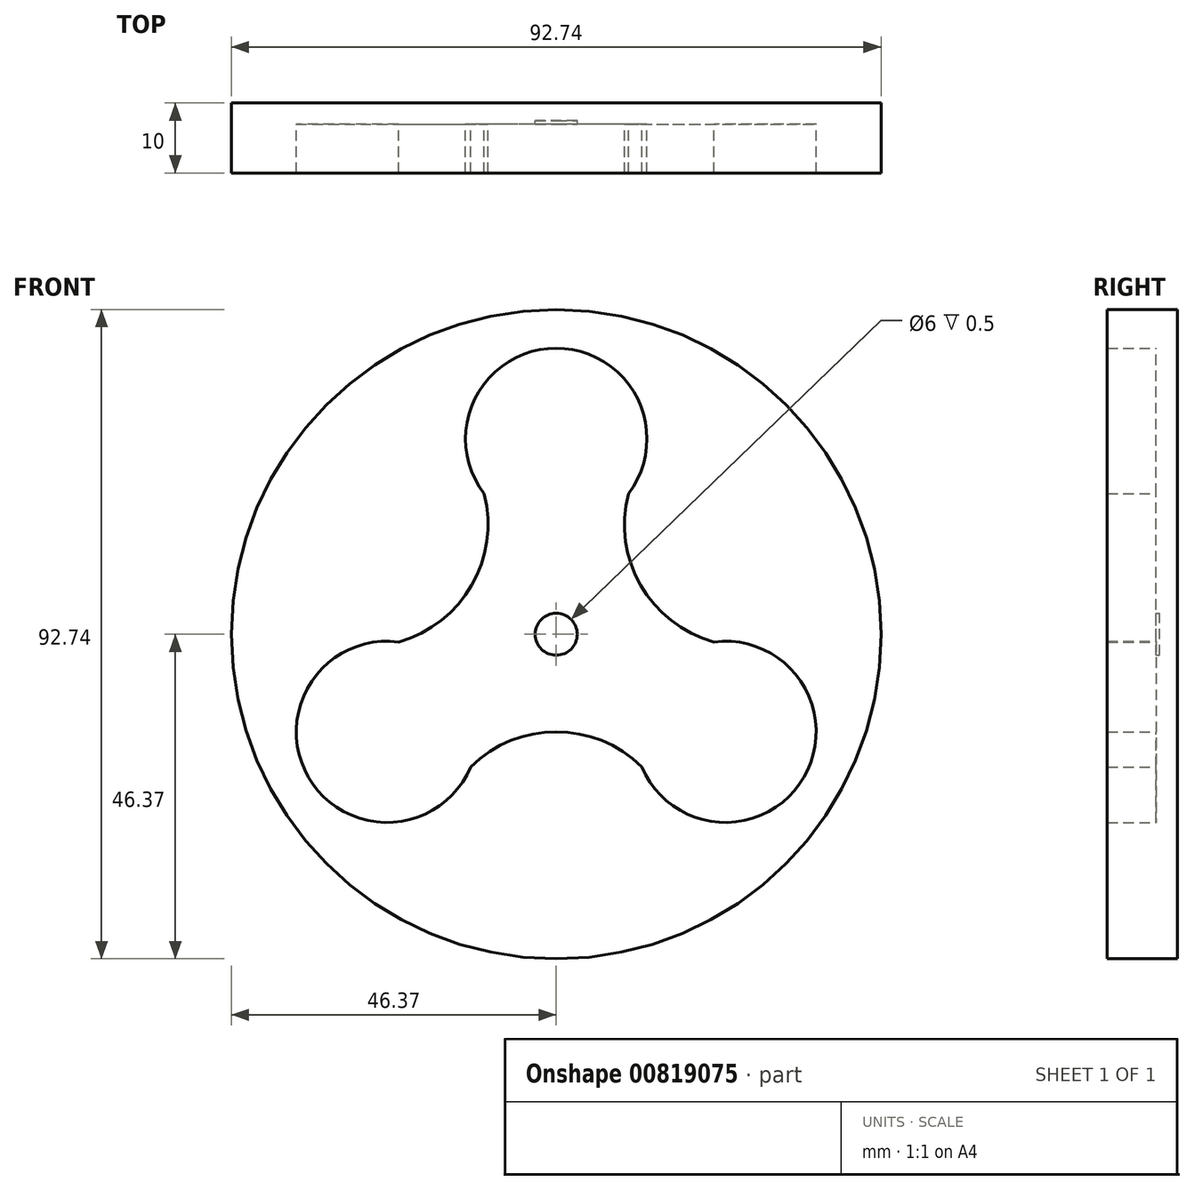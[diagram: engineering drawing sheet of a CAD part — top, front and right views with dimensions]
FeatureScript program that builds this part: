
annotation { "Feature Type Name" : "Feature", "Feature Type Description" : "" }
export const myFeature = defineFeature(function(context is Context, id is Id, definition is map)
    precondition{}
    {
        {
            var Q0;
            Q0=qCreatedBy(makeId("Front.planeOp"),FACE);
            var sketch = newSketch(context, id + "F0", { "sketchPlane" : qUnion([Q0])});
            skCircle(sketch, "E0", {"center": v(0, 0) * mm, "radius": 10.95 * mm});
            skCircle(sketch, "E1.0", {"center": v(0, 0) * mm, "radius": 12.95 * mm});
            skCircle(sketch, "E2", {"center": v(0, 27.9) * mm, "radius": 10.95 * mm});
            skCircle(sketch, "E3.0", {"center": v(0, 27.9) * mm, "radius": 12.95 * mm});
            skCircle(sketch, "E4.1.0", {"center": v(-24.16, -13.95) * mm, "radius": 10.95 * mm});
            skCircle(sketch, "E4.1.1", {"center": v(-24.16, -13.95) * mm, "radius": 12.95 * mm});
            skCircle(sketch, "E4.2.0", {"center": v(24.16, -13.95) * mm, "radius": 10.95 * mm});
            skCircle(sketch, "E4.2.1", {"center": v(24.16, -13.95) * mm, "radius": 12.95 * mm});
            skArc(sketch, "E5", {"start": v(10.3, 20.05) * mm, "mid": v(12.07, 6.97) * mm, "end": v(22.52, -1.1) * mm});
            skArc(sketch, "E6.1.0", {"start": v(-22.52, -1.1) * mm, "mid": v(-12.07, 6.97) * mm, "end": v(-10.3, 20.05) * mm});
            skArc(sketch, "E6.2.0", {"start": v(12.22, -18.95) * mm, "mid": v(0, -13.94) * mm, "end": v(-12.22, -18.95) * mm});
            skCircle(sketch, "E7", {"center": v(0, 0) * mm, "radius": 46.37 * mm});
            skCircle(sketch, "E8", {"center": v(0, 0) * mm, "radius": 2.5 * mm});
            skCircle(sketch, "E9.0", {"center": v(0, 0) * mm, "radius": 3 * mm});
            skSolve(sketch);
        }
        {
            var Q0;
            Q0 = qSketchRegion(id + "F0", true);
            extrude(context, id + "F1", {"entities" : qUnion([Q0]), "depth" : 10 * mm, "offsetDistance" : 25 * mm});
        }
        {
            var Q0;
            Q0=makeQuery(id+"F0.imprint","IMPRINT",FACE,{"disambiguationData":[TD([[makeQuery(id+"F0.imprint","IMPRINT",EDGE,{"derivedFrom":sQuery(id+"F0.wireOp",EDGE,"E0")}),-1.0]])]});
            var Q1;
            Q1=makeQuery(id+"F0.imprint","IMPRINT",FACE,{"disambiguationData":[TD([[makeQuery(id+"F0.imprint","IMPRINT",EDGE,{"derivedFrom":sQuery(id+"F0.wireOp",EDGE,"E1.0")}),-1.0]])]});
            var Q2;
            Q2=makeQuery(id+"F0.imprint","IMPRINT",FACE,{"disambiguationData":[TD([[makeQuery(id+"F0.imprint","IMPRINT",EDGE,{"derivedFrom":sQuery(id+"F0.wireOp",EDGE,"E2")}),1.0]])]});
            var Q3;
            Q3=makeQuery(id+"F0.imprint","IMPRINT",FACE,{"disambiguationData":[TD([[makeQuery(id+"F0.imprint","IMPRINT",EDGE,{"derivedFrom":sQuery(id+"F0.wireOp",EDGE,"E2")}),-1.0]])]});
            var Q4;
            Q4=makeQuery(id+"F0.imprint","IMPRINT",FACE,{"disambiguationData":[TD([[makeQuery(id+"F0.imprint","IMPRINT",EDGE,{"derivedFrom":sQuery(id+"F0.wireOp",EDGE,"E4.2.0")}),-1.0]])]});
            var Q5;
            Q5=makeQuery(id+"F0.imprint","IMPRINT",FACE,{"disambiguationData":[TD([[makeQuery(id+"F0.imprint","IMPRINT",EDGE,{"derivedFrom":sQuery(id+"F0.wireOp",EDGE,"E4.1.0")}),-1.0]])]});
            var Q6;
            Q6=makeQuery(id+"F0.imprint","IMPRINT",FACE,{"disambiguationData":[TD([[makeQuery(id+"F0.imprint","IMPRINT",EDGE,{"derivedFrom":sQuery(id+"F0.wireOp",EDGE,"E0")}),1.0]])]});
            var Q7;
            Q7=makeQuery(id+"F0.imprint","IMPRINT",FACE,{"disambiguationData":[TD([[makeQuery(id+"F0.imprint","IMPRINT",EDGE,{"derivedFrom":sQuery(id+"F0.wireOp",EDGE,"E4.2.0")}),1.0]])]});
            var Q8;
            Q8=makeQuery(id+"F0.imprint","IMPRINT",FACE,{"disambiguationData":[TD([[makeQuery(id+"F0.imprint","IMPRINT",EDGE,{"derivedFrom":sQuery(id+"F0.wireOp",EDGE,"E4.1.0")}),1.0]])]});
            extrude(context, id + "F2", {"entities" : qUnion([Q0, Q1, Q2, Q3, Q4, Q5, Q6, Q7, Q8]), "operationType" : NewBodyOperationType.ADD, "depth" : 3 * mm, "offsetDistance" : 25 * mm});
        }
        {
            var Q0;
            Q0 = qSketchRegion(id + "F0", true);
            var Q1;
            Q1=makeQuery(id+"F0.imprint","IMPRINT",FACE,{"disambiguationData":[TD([[makeQuery(id+"F0.imprint","IMPRINT",EDGE,{"derivedFrom":sQuery(id+"F0.wireOp",EDGE,"E8")}),-1.0]])]});
            var Q2;
            Q2=makeQuery(id+"F0.imprint","IMPRINT",FACE,{"disambiguationData":[TD([[makeQuery(id+"F0.imprint","IMPRINT",EDGE,{"derivedFrom":sQuery(id+"F0.wireOp",EDGE,"E8")}),1.0]])]});
            extrude(context, id + "F3", {"entities" : qUnion([Q0, Q1, Q2]), "operationType" : NewBodyOperationType.ADD, "depth" : 2.5 * mm, "offsetDistance" : 25 * mm});
        }
    });
